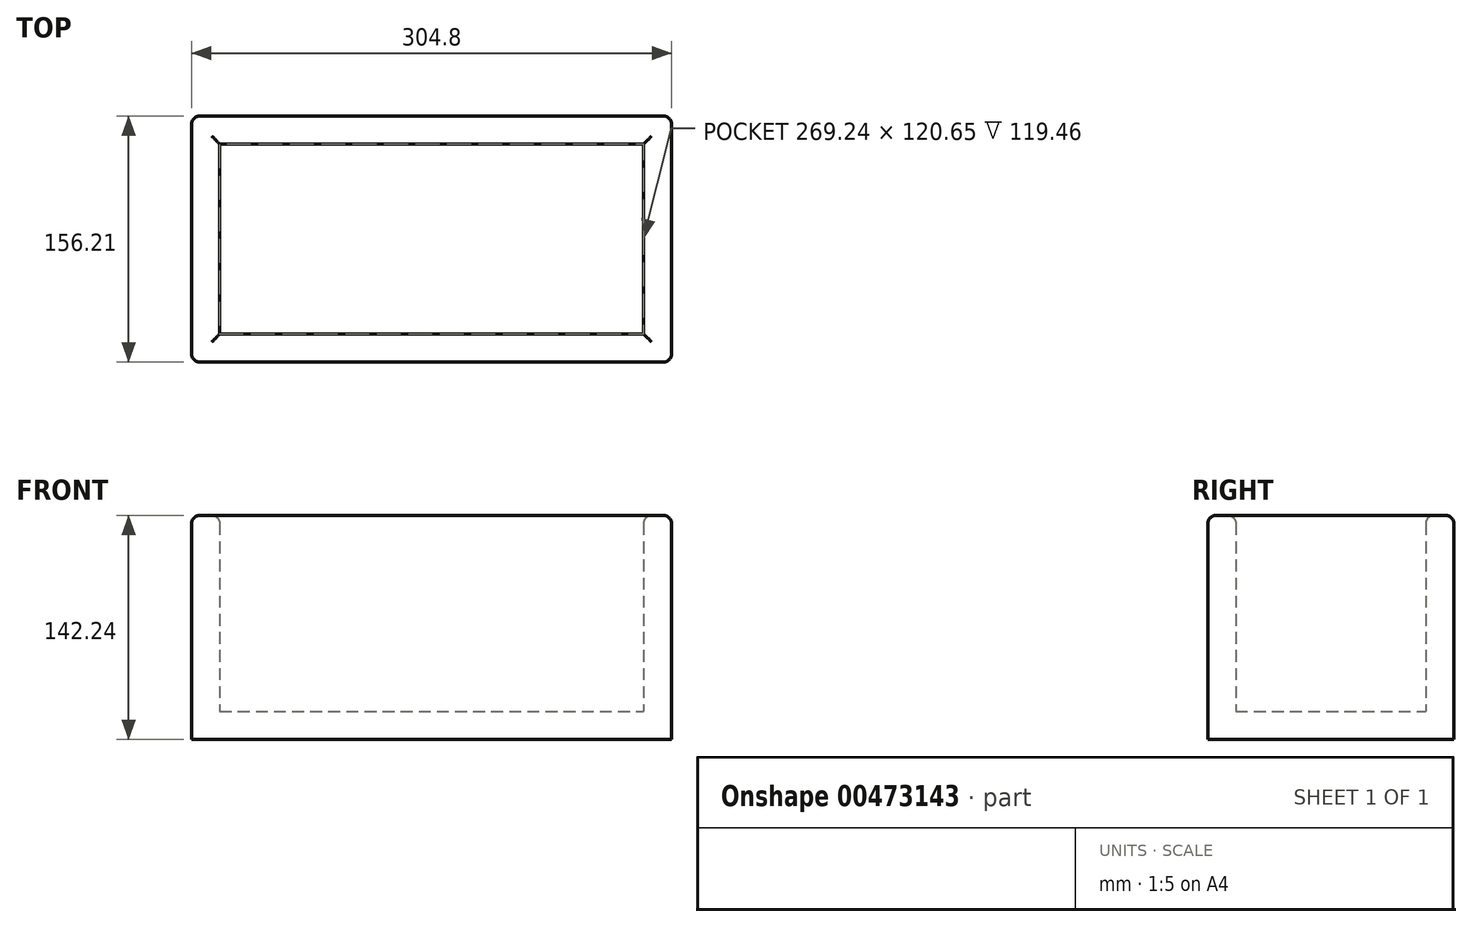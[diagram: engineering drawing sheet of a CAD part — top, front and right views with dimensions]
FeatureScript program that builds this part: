
annotation { "Feature Type Name" : "Feature", "Feature Type Description" : "" }
export const myFeature = defineFeature(function(context is Context, id is Id, definition is map)
    precondition{}
    {
        {
            var Q0;
            Q0=qCreatedBy(makeId("Front.planeOp"),FACE);
            var sketch = newSketch(context, id + "F0", { "sketchPlane" : qUnion([Q0])});
            skLineSegment(sketch, "E0.bottom", {"start": v(-246.49, 76.95) * mm, "end": v(58.31, 76.95) * mm});
            skLineSegment(sketch, "E0.top", {"start": v(-246.49, -65.29) * mm, "end": v(58.31, -65.29) * mm});
            skLineSegment(sketch, "E0.left", {"start": v(-246.49, 76.95) * mm, "end": v(-246.49, -65.29) * mm});
            skLineSegment(sketch, "E0.right", {"start": v(58.31, 76.95) * mm, "end": v(58.31, -65.29) * mm});
            skSolve(sketch);
        }
        {
            var Q0;
            Q0=makeQuery(id+"F0.imprint","IMPRINT",FACE,{"disambiguationData":[TD([[makeQuery(id+"F0.imprint","IMPRINT",EDGE,{"derivedFrom":sQuery(id+"F0.wireOp",EDGE,"E0.bottom")}),-1.0]])]});
            extrude(context, id + "F1", {"entities" : qUnion([Q0]), "depth" : 156.2 * mm});
        }
        {
            var Q0;
            Q0=makeQuery(id+"F1.opExtrude","SWEPT_FACE",FACE,{"disambiguationData":[OSD([sQuery(id+"F0.wireOp",EDGE,"E0.bottom")])]});
            shell(context, id + "F2", {"entities" : qUnion([Q0]), "thickness" : 17.78 * mm});
        }
        {
            var Q0;
            Q0=makeQuery(id+"F1.opExtrude","SWEPT_BODY",BODY,{"disambiguationData":[OSD([sQuery(id+"F0.wireOp",EDGE,"E0.bottom"),sQuery(id+"F0.wireOp",EDGE,"E0.top"),sQuery(id+"F0.wireOp",EDGE,"E0.left"),sQuery(id+"F0.wireOp",EDGE,"E0.right")])]});
            var Q1;
            Q1=makeQuery(id+"F1.opExtrude","CAP_VERTEX",VERTEX,{"disambiguationData":[OSD([sQuery(id+"F0.wireOp",EDGE,"E0.bottom"),sQuery(id+"F0.wireOp",EDGE,"E0.left")])],"isStart":true});
            var Q2;
            {var subQ0=sQuery(id+"F0.wireOp",EDGE,"E0.left");var subQ1=sQuery(id+"F0.wireOp",EDGE,"E0.bottom");Q2=makeQuery(id+"F2.opShell","OFFSET_VERTEX",VERTEX,{"disambiguationData":[OSD([subQ1,subQ0]),TDD([makeQuery(id+"F1.opExtrude","CAP_VERTEX",VERTEX,{"disambiguationData":[OSD([subQ1,subQ0])],"isStart":true})])]});}
            var Q3;
            Q3=qCreatedBy(makeId("Top.planeOp"),FACE);
            transform(context, id + "F3", {"entities" : qUnion([Q0]), "transformType" : TransformType.TRANSLATION_DISTANCE, "transformDirection" : qUnion([Q3]), "distance" : 77.98 * mm, "oppositeDirection" : true, "makeCopy" : false});
        }
        {
            var Q0;
            Q0=makeQuery(id+"F1.opExtrude","CAP_EDGE",EDGE,{"disambiguationData":[OSD([sQuery(id+"F0.wireOp",EDGE,"E0.bottom")])],"isStart":false});
            var Q1;
            Q1=makeQuery(id+"F1.opExtrude","SWEPT_EDGE",EDGE,{"disambiguationData":[OSD([sQuery(id+"F0.wireOp",EDGE,"E0.bottom"),sQuery(id+"F0.wireOp",EDGE,"E0.left")])]});
            var Q2;
            Q2=makeQuery(id+"F1.opExtrude","CAP_EDGE",EDGE,{"disambiguationData":[OSD([sQuery(id+"F0.wireOp",EDGE,"E0.bottom")])],"isStart":true});
            var Q3;
            Q3=makeQuery(id+"F1.opExtrude","SWEPT_EDGE",EDGE,{"disambiguationData":[OSD([sQuery(id+"F0.wireOp",EDGE,"E0.bottom"),sQuery(id+"F0.wireOp",EDGE,"E0.right")])]});
            var Q4;
            Q4=makeQuery(id+"F2.opShell","OFFSET_EDGE",EDGE,{"disambiguationData":[OSD([sQuery(id+"F0.wireOp",EDGE,"E0.bottom"),sQuery(id+"F0.wireOp",EDGE,"E0.right")])]});
            var Q5;
            {var subQ0=sQuery(id+"F0.wireOp",EDGE,"E0.bottom");Q5=makeQuery(id+"F2.opShell","OFFSET_EDGE",EDGE,{"disambiguationData":[OSD([subQ0]),TDD([makeQuery(id+"F1.opExtrude","CAP_EDGE",EDGE,{"disambiguationData":[OSD([subQ0])],"isStart":false})])]});}
            var Q6;
            {var subQ0=sQuery(id+"F0.wireOp",EDGE,"E0.bottom");Q6=makeQuery(id+"F2.opShell","OFFSET_EDGE",EDGE,{"disambiguationData":[OSD([subQ0]),TDD([makeQuery(id+"F1.opExtrude","CAP_EDGE",EDGE,{"disambiguationData":[OSD([subQ0])],"isStart":true})])]});}
            var Q7;
            Q7=makeQuery(id+"F2.opShell","OFFSET_EDGE",EDGE,{"disambiguationData":[OSD([sQuery(id+"F0.wireOp",EDGE,"E0.bottom"),sQuery(id+"F0.wireOp",EDGE,"E0.left")])]});
            var Q8;
            Q8=makeQuery(id+"F1.opExtrude","CAP_EDGE",EDGE,{"disambiguationData":[OSD([sQuery(id+"F0.wireOp",EDGE,"E0.left")])],"isStart":false});
            var Q9;
            Q9=makeQuery(id+"F1.opExtrude","CAP_EDGE",EDGE,{"disambiguationData":[OSD([sQuery(id+"F0.wireOp",EDGE,"E0.right")])],"isStart":false});
            var Q10;
            Q10=makeQuery(id+"F1.opExtrude","CAP_EDGE",EDGE,{"disambiguationData":[OSD([sQuery(id+"F0.wireOp",EDGE,"E0.left")])],"isStart":true});
            var Q11;
            Q11=makeQuery(id+"F1.opExtrude","CAP_EDGE",EDGE,{"disambiguationData":[OSD([sQuery(id+"F0.wireOp",EDGE,"E0.right")])],"isStart":true});
            fillet(context, id + "F4", {"entities" : qUnion([Q0, Q1, Q2, Q3, Q4, Q5, Q6, Q7, Q8, Q9, Q10, Q11]), "radius" : 5 * mm, "tangentPropagation" : true, "allowEdgeOverflow" : false});
        }
    });
